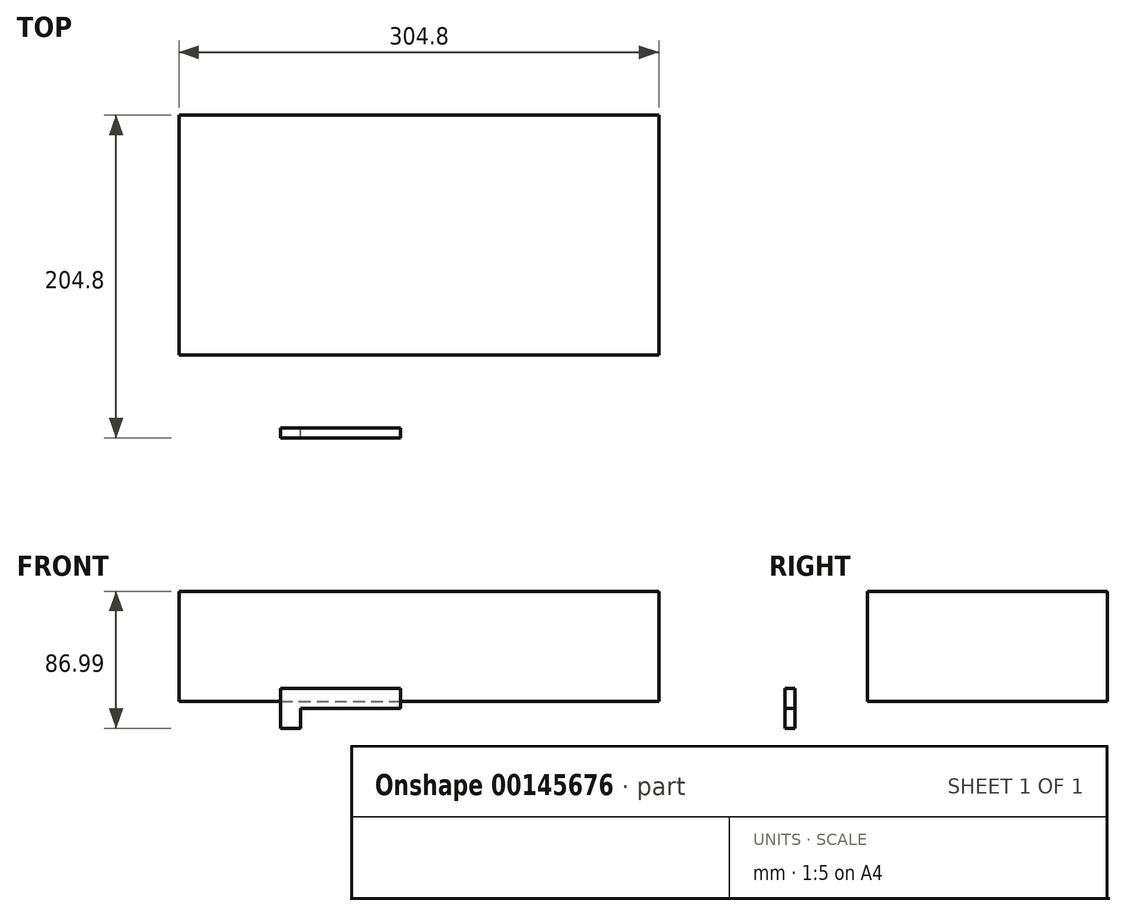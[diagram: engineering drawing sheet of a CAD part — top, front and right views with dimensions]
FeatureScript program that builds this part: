
annotation { "Feature Type Name" : "Feature", "Feature Type Description" : "" }
export const myFeature = defineFeature(function(context is Context, id is Id, definition is map)
    precondition{}
    {
        {
            var Q0;
            Q0=qCreatedBy(makeId("Front.planeOp"),FACE);
            var sketch = newSketch(context, id + "F0", { "sketchPlane" : qUnion([Q0])});
            skLineSegment(sketch, "E0", {"start": v(-47.66, -17.14) * mm, "end": v(-47.66, 8.26) * mm});
            skLineSegment(sketch, "E1", {"start": v(-47.66, 8.26) * mm, "end": v(28.54, 8.26) * mm});
            skLineSegment(sketch, "E2", {"start": v(28.54, 8.26) * mm, "end": v(28.54, -4.44) * mm});
            skLineSegment(sketch, "E3", {"start": v(28.54, -4.44) * mm, "end": v(-34.96, -4.44) * mm});
            skLineSegment(sketch, "E4", {"start": v(-34.96, -4.44) * mm, "end": v(-34.96, -17.14) * mm});
            skLineSegment(sketch, "E5", {"start": v(-34.96, -17.14) * mm, "end": v(-47.66, -17.14) * mm});
            skSolve(sketch);
        }
        {
            var Q0;
            Q0=makeQuery(id+"F0.imprint","IMPRINT",FACE,{"disambiguationData":[TD([[makeQuery(id+"F0.imprint","IMPRINT",EDGE,{"derivedFrom":sQuery(id+"F0.wireOp",EDGE,"E0")}),-1.0]])]});
            extrude(context, id + "F1", {"entities" : qUnion([Q0]), "depth" : 6.35 * mm});
        }
        {
            var Q0;
            Q0=qCreatedBy(makeId("Top.planeOp"),FACE);
            var sketch = newSketch(context, id + "F2", { "sketchPlane" : qUnion([Q0])});
            skLineSegment(sketch, "E6.bottom", {"start": v(-112.2, 46.05) * mm, "end": v(192.6, 46.05) * mm});
            skLineSegment(sketch, "E6.top", {"start": v(-112.2, 198.45) * mm, "end": v(192.6, 198.45) * mm});
            skLineSegment(sketch, "E6.left", {"start": v(-112.2, 46.05) * mm, "end": v(-112.2, 198.45) * mm});
            skLineSegment(sketch, "E6.right", {"start": v(192.6, 46.05) * mm, "end": v(192.6, 198.45) * mm});
            skSolve(sketch);
        }
        {
            var Q0;
            Q0=makeQuery(id+"F2.imprint","IMPRINT",FACE,{"disambiguationData":[TD([[makeQuery(id+"F2.imprint","IMPRINT",EDGE,{"derivedFrom":sQuery(id+"F2.wireOp",EDGE,"E6.bottom")}),1.0]])]});
            extrude(context, id + "F3", {"entities" : qUnion([Q0]), "depth" : 69.85 * mm});
        }
    });
